# Revit family: ASSA_ABLOY_Transparent
name_source: partatom
category: Doors
units: mm (PartAtom-declared; Revit-internal decimal feet)

## family parameters
Always vertical = Yes
Cut with Voids When Loaded = No
Host = Wall
Room Calculation Point = No
Shared = No

## types (1)
- Transparent
    AccessoryOptions = Contact manufacturer
    Analytic Construction = <None>
    AntiFingerTrapRequirement = No
    Capacity = 1 x 5 - 7
    Colour = Customer specific
    Construction Type = Sliding Door
    Default Elevation = 0 mm  [stored 0 ft]
    Define Thermal Properties by = Schematic Type
    Description = Automatic sliding door system
    DoorIncluded = Yes
    DoorSeal = Yes
    DoorsetFasteners = Screws
    DoorsetOperation = Automatic
    DoorsetOptions = Sliding door system
    ElectronicLock = Yes
    FireExit = No
    Frame Material = -
    FrameFinishOptions = Powder coated, Anodized, Clad in stainless steel, etc.
    FrameProfile = Aluminium
    FrameSeal = Yes
    GlassLayers = 0
    GlassThickness1 = 6 mm  [stored 0.019685 ft]
    GlassThickness2 = 40 mm  [stored 0.131234 ft]
    GlassType = 6 mm laminated
    HandicapAccessible = Yes
    HasDrive = Yes
    Infiltration = 0
    IsExternal = Yes
    LeafColourOptions = All RAL, customer specific
    Manufacturer = ASSA ABLOY
    ManufacturerURL = http://www.assaabloyentrance.com
    Material = Aluminium
    Model = Transparent
    ModelReference = Depends on the configuration
    NominalHeight = 3000 mm  [stored 9.84252 ft]
    NominalLength = 198 mm  [stored 0.649606 ft]
    NominalWidth = 6000 mm
    OperatingTemperature = -20º to +50ºC
    ReplacementCost = Depends on the configuration and door type
    SafetyDevices = Fully compliant with EN16005 and EN ISO 13849-1
    SelfClosing = Yes
    SerialNumber = 800327
    ServiceLifeDuration = 10 years
    Shape = Rectangular shaped
    SmokeStop = No
    ThermalTransmittance = 0
    ThresholdRequired = No
    URL = https://www.assaabloyentrance.com
    Uniclass2 = Ss_25_30_20_77
    WarrantyDescription = Depends on country
    Weight = Depends on configuration and size

note: [stored X ft] marks values corroborated as IEEE doubles in the binary element streams (Revit-internal decimal feet)

## geometry (parser evidence)
native form markers: Sweep x32
no freeform markers — native parametric forms only
